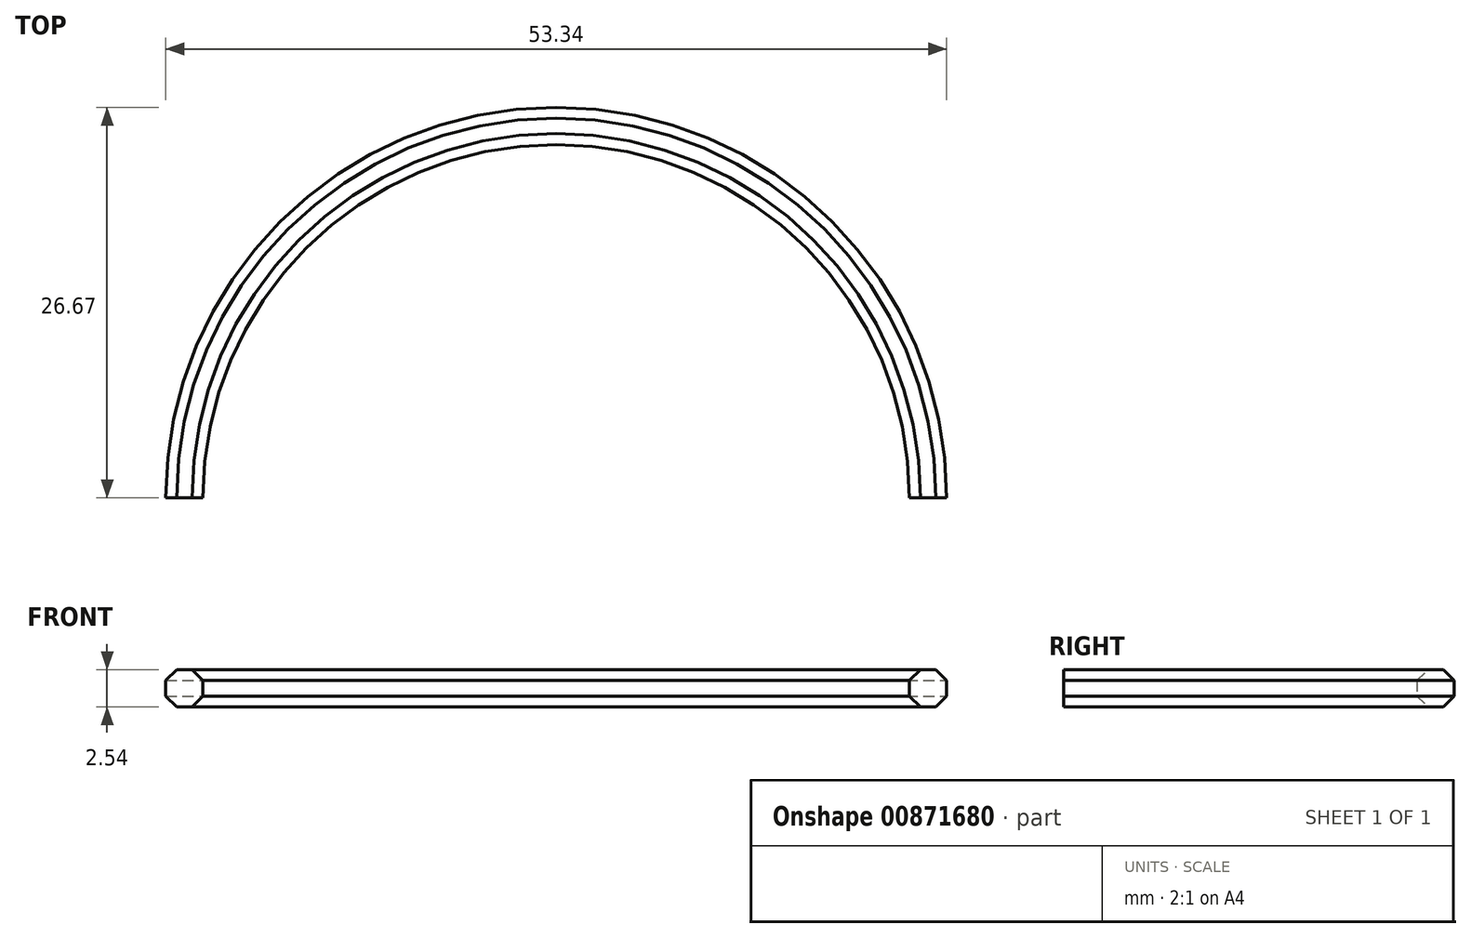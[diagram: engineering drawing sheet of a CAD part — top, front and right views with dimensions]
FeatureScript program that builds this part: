
annotation { "Feature Type Name" : "Feature", "Feature Type Description" : "" }
export const myFeature = defineFeature(function(context is Context, id is Id, definition is map)
    precondition{}
    {
        {
            var Q0;
            Q0=qCreatedBy(makeId("Front.planeOp"),FACE);
            var sketch = newSketch(context, id + "F0", { "sketchPlane" : qUnion([Q0])});
            skLineSegment(sketch, "E0", {"start": v(0, 0) * mm, "end": v(0, 14.17) * mm, "construction": true});
            skLineSegment(sketch, "E1.0", {"start": v(24.87, 1.27) * mm, "end": v(25.93, 1.27) * mm});
            skLineSegment(sketch, "E1.1", {"start": v(25.93, 1.27) * mm, "end": v(26.67, 0.53) * mm});
            skLineSegment(sketch, "E1.2", {"start": v(26.67, 0.53) * mm, "end": v(26.67, -0.53) * mm});
            skLineSegment(sketch, "E1.3", {"start": v(26.67, -0.53) * mm, "end": v(25.93, -1.27) * mm});
            skLineSegment(sketch, "E1.4", {"start": v(25.93, -1.27) * mm, "end": v(24.87, -1.27) * mm});
            skLineSegment(sketch, "E1.5", {"start": v(24.87, -1.27) * mm, "end": v(24.13, -0.53) * mm});
            skLineSegment(sketch, "E1.6", {"start": v(24.13, -0.53) * mm, "end": v(24.13, 0.53) * mm});
            skLineSegment(sketch, "E1.7", {"start": v(24.13, 0.53) * mm, "end": v(24.87, 1.27) * mm});
            skPoint(sketch, "E1.0.midPoint", {"position": v(25.4, 1.27) * mm});
            skSolve(sketch);
        }
        {
            var Q0;
            Q0=makeQuery(id+"F0.imprint","IMPRINT",FACE,{"disambiguationData":[TD([[makeQuery(id+"F0.imprint","IMPRINT",EDGE,{"derivedFrom":sQuery(id+"F0.wireOp",EDGE,"35YtdCXk-rYZG-fsQI-9mTP-38sCpzBk6uY4")}),1.0]])]});
            var Q1;
            Q1=makeQuery(id+"F0.imprint","IMPRINT",FACE,{"disambiguationData":[TD([[makeQuery(id+"F0.imprint","IMPRINT",EDGE,{"derivedFrom":sQuery(id+"F0.wireOp",EDGE,"E1.0")}),-1.0]])]});
            var Q2;
            Q2=sQuery(id+"F0.wireOp",EDGE,"E0");
            revolve(context, id + "F1", {"surfaceOperationType" : NewSurfaceOperationType.NEW, "entities" : qUnion([Q0, Q1]), "axis" : qUnion([Q2]), "revolveType" : RevolveType.ONE_DIRECTION, "angle" : 180 * degree});
        }
    });
